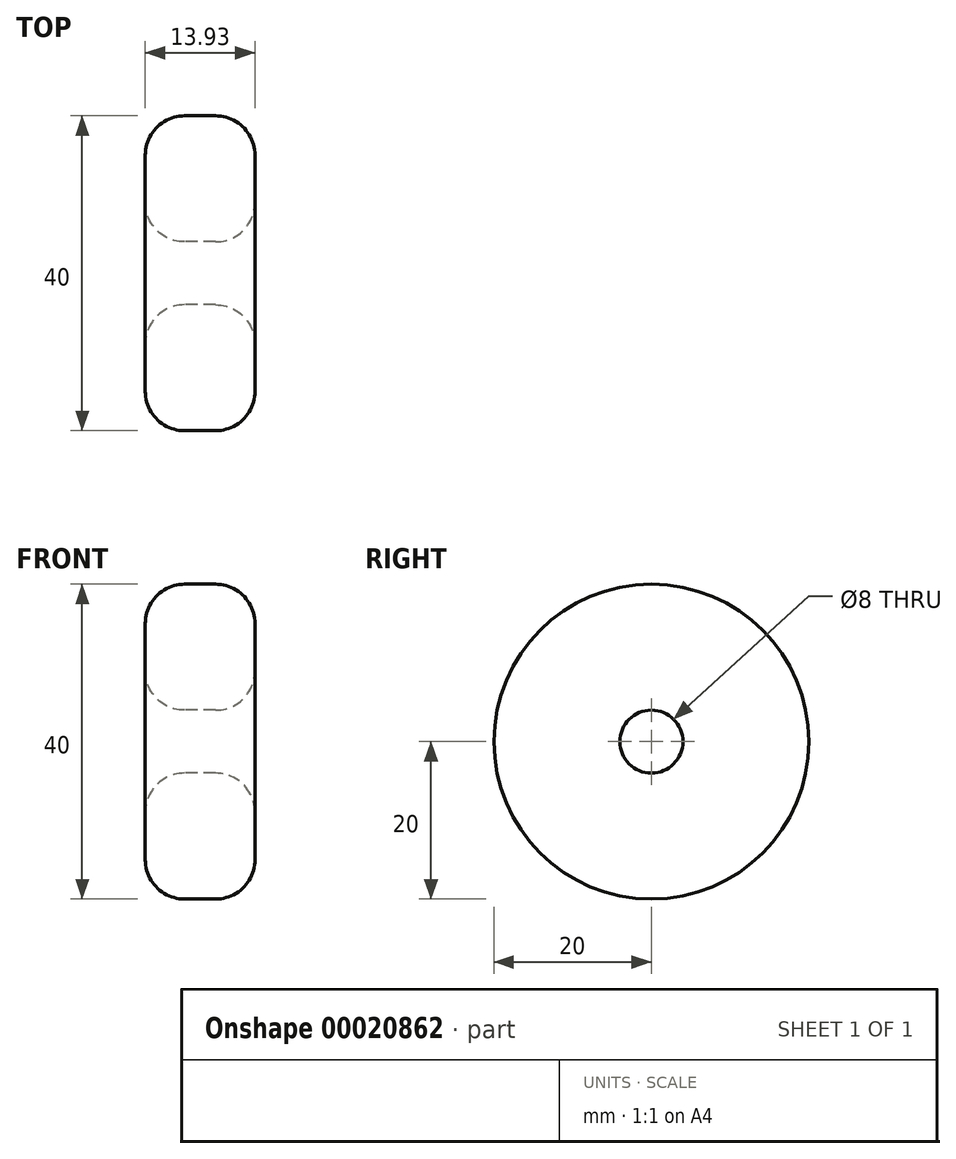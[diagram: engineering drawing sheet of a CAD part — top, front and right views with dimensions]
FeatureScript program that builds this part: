
annotation { "Feature Type Name" : "Feature", "Feature Type Description" : "" }
export const myFeature = defineFeature(function(context is Context, id is Id, definition is map)
    precondition{}
    {
        {
            var Q0;
            Q0=qCreatedBy(makeId("Right.planeOp"),FACE);
            var sketch = newSketch(context, id + "F0", { "sketchPlane" : qUnion([Q0])});
            skCircle(sketch, "E0", {"center": v(0, 0) * mm, "radius": 4 * mm});
            skCircle(sketch, "E1", {"center": v(0, 0) * mm, "radius": 20 * mm});
            skSolve(sketch);
        }
        {
            var Q0;
            Q0 = qSketchRegion(id + "F0", true);
            extrude(context, id + "F1", {"entities" : qUnion([Q0]), "depth" : 13.93 * mm});
        }
        {
            var Q0;
            Q0=makeQuery(id+"F1.opExtrude","CAP_EDGE",EDGE,{"disambiguationData":[OSD([sQuery(id+"F0.wireOp",EDGE,"E1")])],"isStart":false});
            var Q1;
            Q1=makeQuery(id+"F1.opExtrude","CAP_EDGE",EDGE,{"disambiguationData":[OSD([sQuery(id+"F0.wireOp",EDGE,"E1")])],"isStart":true});
            var Q2;
            Q2=makeQuery(id+"F1.opExtrude","CAP_EDGE",EDGE,{"disambiguationData":[OSD([sQuery(id+"F0.wireOp",EDGE,"E0")])],"isStart":false});
            var Q3;
            Q3=makeQuery(id+"F1.opExtrude","CAP_EDGE",EDGE,{"disambiguationData":[OSD([sQuery(id+"F0.wireOp",EDGE,"E0")])],"isStart":true});
            fillet(context, id + "F2", {"entities" : qUnion([Q0, Q1, Q2, Q3]), "radius" : 5 * mm, "tangentPropagation" : true, "allowEdgeOverflow" : false});
        }
    });
